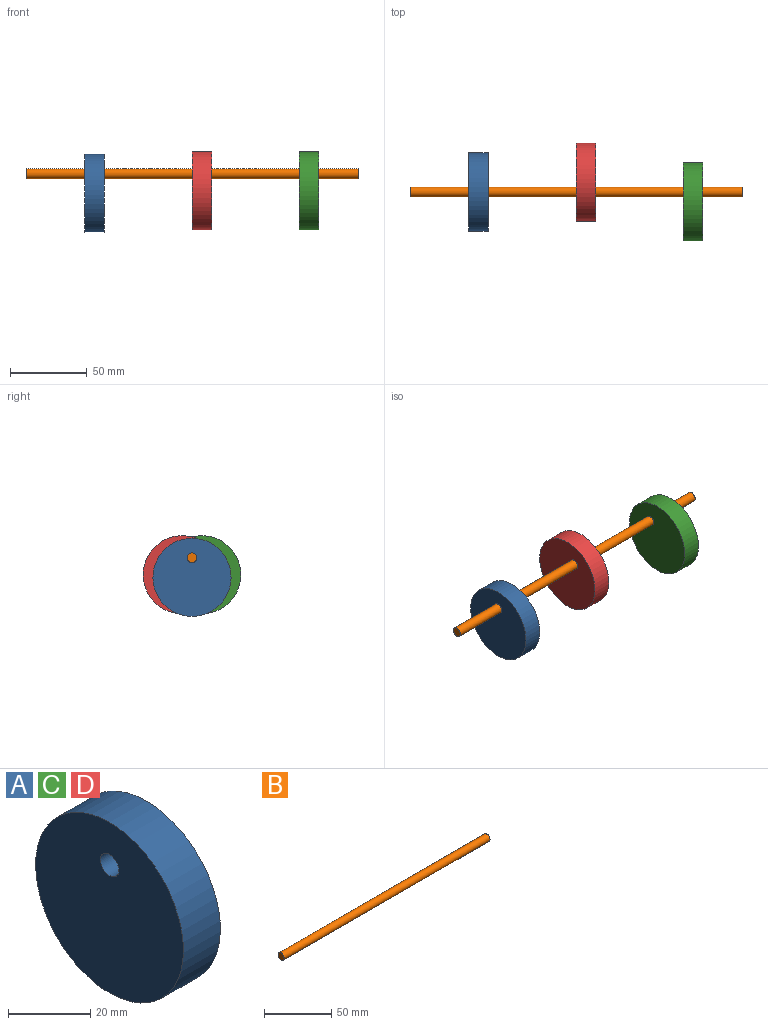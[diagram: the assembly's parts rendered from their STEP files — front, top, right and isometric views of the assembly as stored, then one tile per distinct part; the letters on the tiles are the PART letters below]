
ASSEMBLY  parts=4 mates=3
PART A: 4 faces, bbox 12.7x50.8x50.8 mm
  f0: plane 50.8x50.8mm, normal (-1,0,0), area 1995.2mm2, adj f1,f3
  f1: cylinder r=25.4mm len=50.8mm, axis (-1,0,0), area 2026.8mm2, adj f0,f2
  f2: plane 50.8x50.8mm, normal (1,0,0), area 1995.2mm2, adj f1,f3
  f3: cylinder r=3.17mm len=12.7mm, axis (1,0,0), area 253.4mm2, adj f0,f2
PART B: 3 faces, bbox 215.9x6.4x6.4 mm
  f0: plane 6.35x6.35mm, normal (1,0,0), area 31.7mm2, adj f2
  f1: plane 6.35x6.35mm, normal (-1,0,0), area 31.7mm2, adj f2
  f2: cylinder r=3.17mm len=215.9mm, axis (1,0,0), area 4307mm2, adj f0,f1
PART C: same geometry as A
PART D: same geometry as A
PLACE A t=(12.7,0,-57.15)mm
PLACE B t=(12.7,0,-57.15)mm
PLACE C rot(axis=(-1,0,0),30deg) t=(152.4,-28.58,-49.49)mm
PLACE D rot(axis=(1,0,0),30deg) t=(82.55,28.58,-49.49)mm
MATE fastened D.f3 <-> B.f2  axis (1,0,0) through (114.3,0,0)mm
MATE fastened C.f3 <-> B.f2  axis (1,0,0) through (184.15,0,0)mm
MATE fastened A.f3 <-> B.f2  axis (1,0,0) through (44.45,0,0)mm
